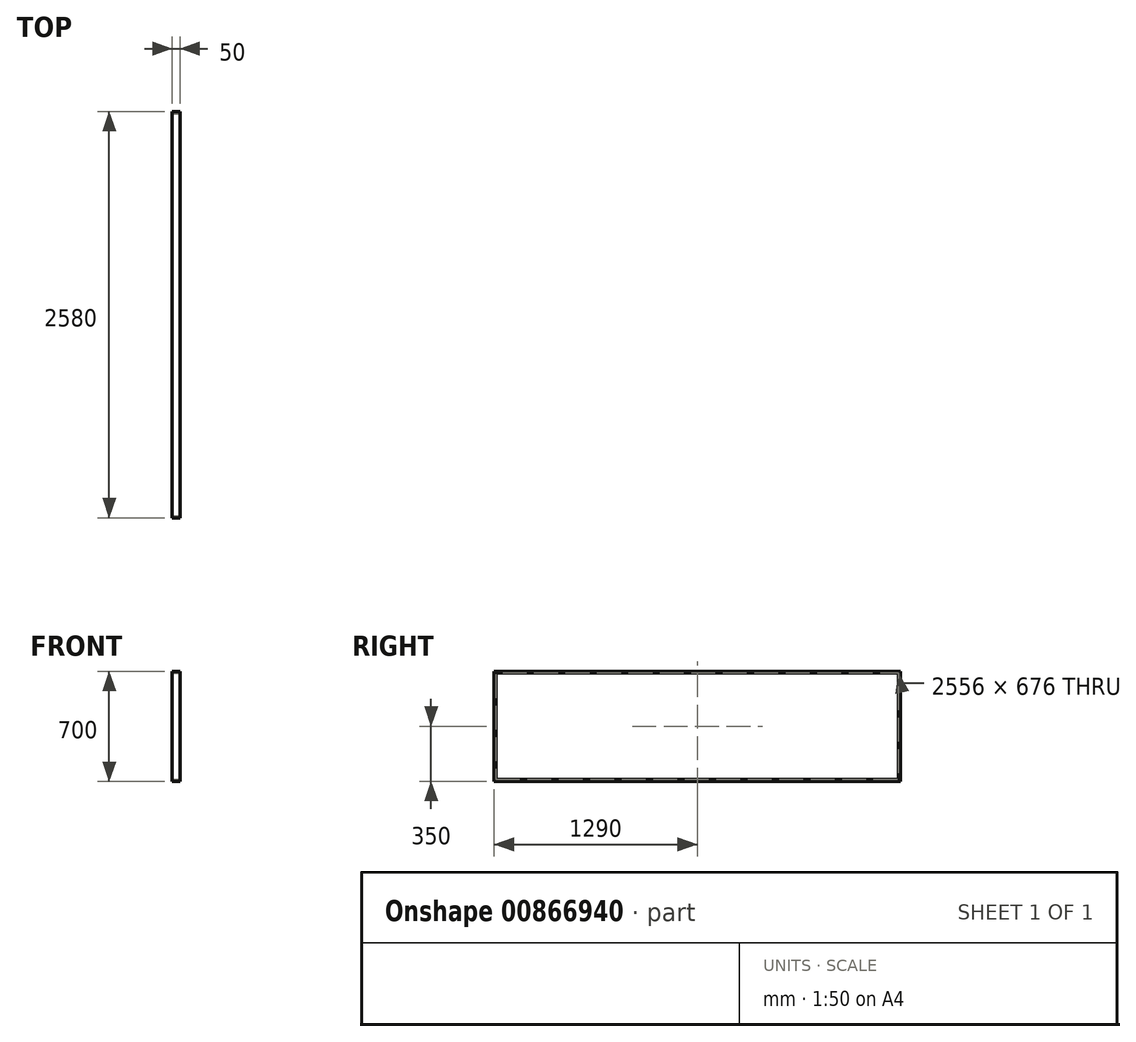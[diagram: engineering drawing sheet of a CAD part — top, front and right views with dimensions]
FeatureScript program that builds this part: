
annotation { "Feature Type Name" : "Feature", "Feature Type Description" : "" }
export const myFeature = defineFeature(function(context is Context, id is Id, definition is map)
    precondition{}
    {
        {
            var Q0;
            Q0=qCreatedBy(makeId("Right.planeOp"),FACE);
            var sketch = newSketch(context, id + "F0", { "sketchPlane" : qUnion([Q0])});
            skLineSegment(sketch, "E0.bottom", {"start": v(-1290, 350) * mm, "end": v(1290, 350) * mm});
            skLineSegment(sketch, "E0.top", {"start": v(-1290, -350) * mm, "end": v(1290, -350) * mm});
            skLineSegment(sketch, "E0.left", {"start": v(-1290, 350) * mm, "end": v(-1290, -350) * mm});
            skLineSegment(sketch, "E0.right", {"start": v(1290, 350) * mm, "end": v(1290, -350) * mm});
            skLineSegment(sketch, "E1.bottom", {"start": v(-1278, 338) * mm, "end": v(1278, 338) * mm});
            skLineSegment(sketch, "E1.top", {"start": v(-1278, -338) * mm, "end": v(1278, -338) * mm});
            skLineSegment(sketch, "E1.left", {"start": v(-1278, 338) * mm, "end": v(-1278, -338) * mm});
            skLineSegment(sketch, "E1.right", {"start": v(1278, 338) * mm, "end": v(1278, -338) * mm});
            skPoint(sketch, "E2", {"position": v(0, -338) * mm});
            skPoint(sketch, "E3", {"position": v(1278, 0) * mm});
            skSolve(sketch);
        }
        {
            var Q0;
            Q0 = qSketchRegion(id + "F0", true);
            extrude(context, id + "F1", {"entities" : qUnion([Q0]), "oppositeDirection" : true, "depth" : 50 * mm, "offsetDistance" : 25 * mm});
        }
    });
